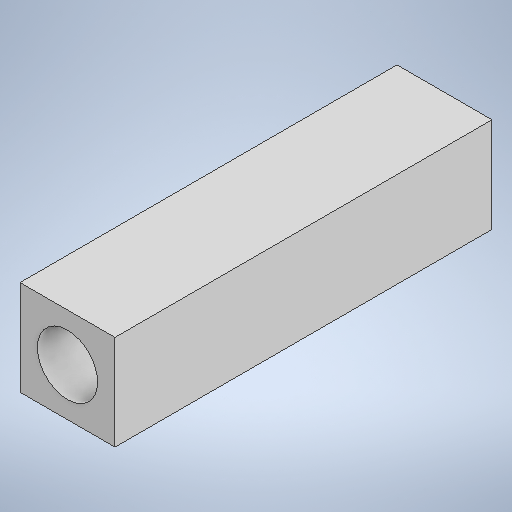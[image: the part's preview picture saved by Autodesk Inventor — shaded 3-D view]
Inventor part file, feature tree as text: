
AUTODESK INVENTOR PART (.ipt)
format: ipt  version: 2025 (Build 290162000, 162)  size: 201,728 bytes
history: native  units: in
note: dims shown in document units (in); Inventor stores cm internally (conversion verified against a paired STEP export)
features: extrude x3, sketch x3
ambient origin geometry x8: Origin, YZ Plane, XZ Plane, XY Plane, X Axis, Y Axis, Z Axis, Center Point
bodies: Solid1 (feature_tree)
feature tree (6):
  extrude  "Extrusion1"  Depth=0.6299in
  extrude  "Extrusion2"  Depth=2.5in
  extrude  "Extrusion3"  Depth=2.3031in
  sketch  "Sketch1"  dims[d0=0.6299in d1=0.6299in]
  sketch  "Sketch2"  dims[d2=2.5in d3=0.0in d4=0.3996in]
  sketch  "Sketch3"  dims[d5=2.3031in d6=0.0in d7=0.315in d8=1.7717in d9=0.0in]
